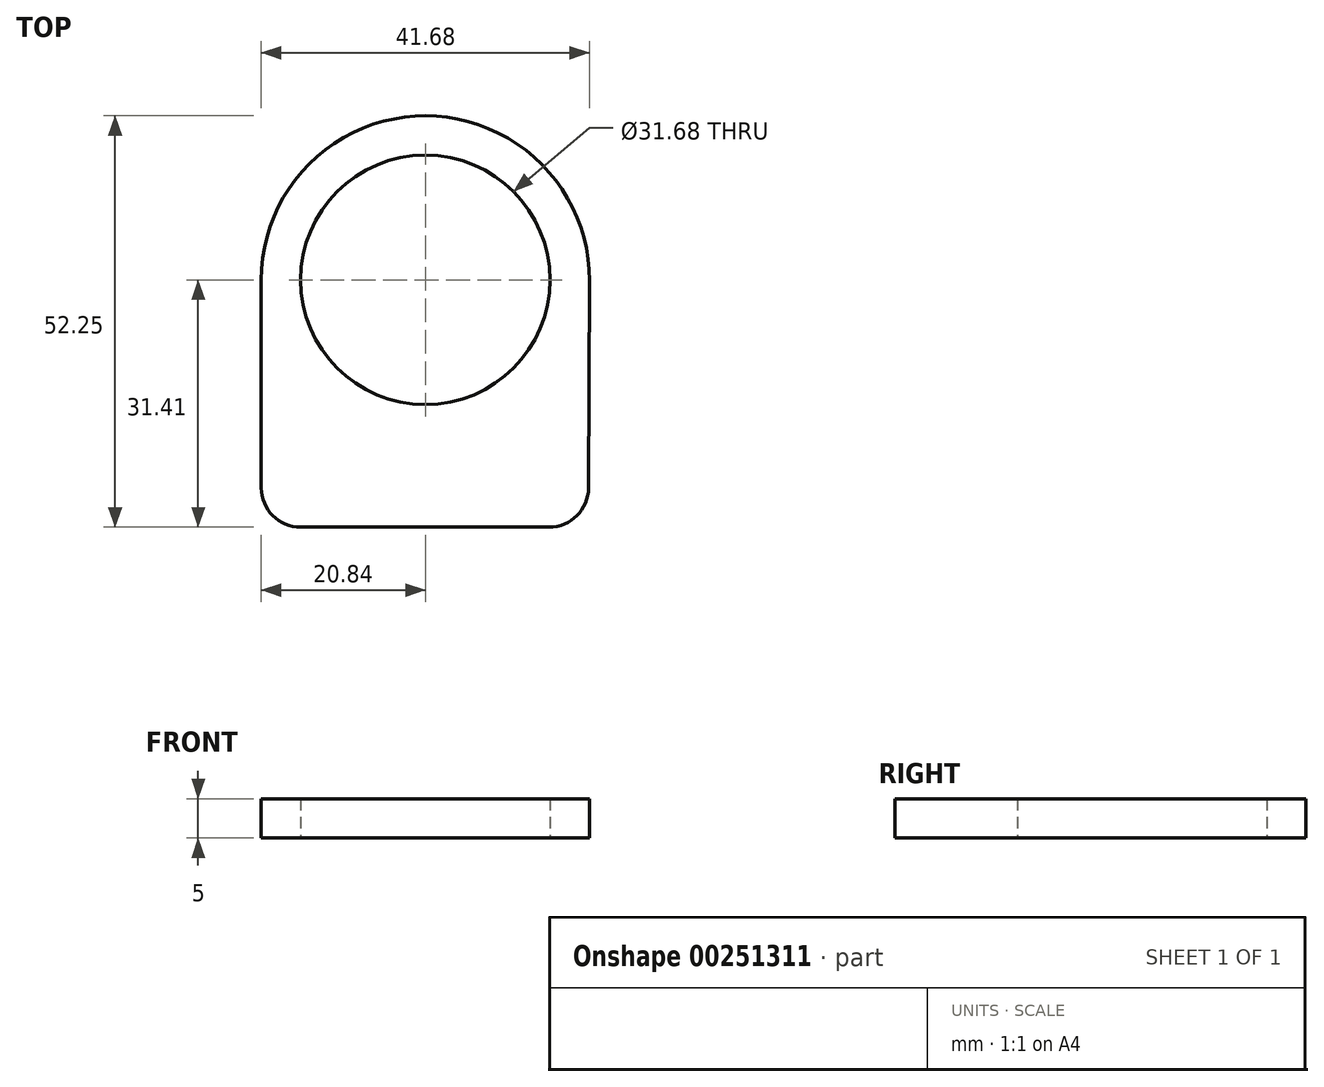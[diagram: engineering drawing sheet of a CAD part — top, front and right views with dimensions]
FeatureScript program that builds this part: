
annotation { "Feature Type Name" : "Feature", "Feature Type Description" : "" }
export const myFeature = defineFeature(function(context is Context, id is Id, definition is map)
    precondition{}
    {
        {
            var Q0;
            Q0=qCreatedBy(makeId("Top.planeOp"),FACE);
            var sketch = newSketch(context, id + "F0", { "sketchPlane" : qUnion([Q0])});
            skCircle(sketch, "E0", {"center": v(0, 0) * mm, "radius": 15.84 * mm});
            skArc(sketch, "E1.0", {"start": v(20.84, -0.09) * mm, "mid": v(0.04, 20.84) * mm, "end": v(-20.84, 0) * mm});
            skLineSegment(sketch, "E2", {"start": v(-20.84, 0) * mm, "end": v(-20.84, -26.41) * mm});
            skLineSegment(sketch, "E3", {"start": v(-15.84, -31.41) * mm, "end": v(15.73, -31.41) * mm});
            skLineSegment(sketch, "E4", {"start": v(20.73, -26.43) * mm, "end": v(20.84, 0) * mm});
            skPoint(sketch, "E5.visualSharp", {"position": v(-20.84, -31.41) * mm});
            skArc(sketch, "E5.filletArc", {"start": v(-20.84, -26.41) * mm, "mid": v(-19.38, -29.95) * mm, "end": v(-15.84, -31.41) * mm});
            skPoint(sketch, "E6.visualSharp", {"position": v(20.7, -31.41) * mm});
            skArc(sketch, "E6.filletArc", {"start": v(15.73, -31.41) * mm, "mid": v(19.26, -29.95) * mm, "end": v(20.73, -26.43) * mm});
            skSolve(sketch);
        }
        {
            var Q0;
            Q0=makeQuery(id+"F0.imprint","IMPRINT",FACE,{"disambiguationData":[TD([[makeQuery(id+"F0.imprint","IMPRINT",EDGE,{"derivedFrom":sQuery(id+"F0.wireOp",EDGE,"E0")}),-1.0]])]});
            extrude(context, id + "F1", {"entities" : qUnion([Q0]), "depth" : 5 * mm, "offsetDistance" : 25 * mm});
        }
    });
